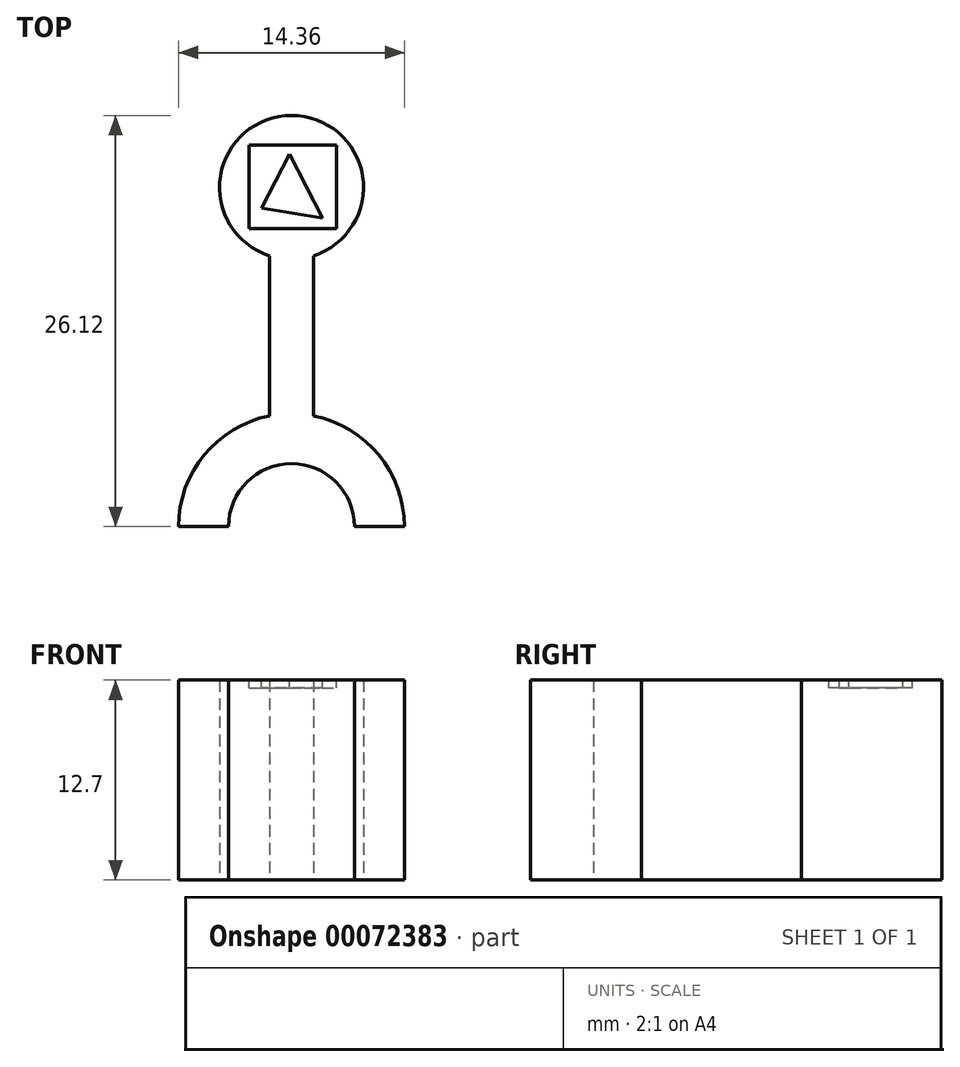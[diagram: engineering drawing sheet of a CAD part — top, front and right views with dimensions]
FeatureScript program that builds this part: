
annotation { "Feature Type Name" : "Feature", "Feature Type Description" : "" }
export const myFeature = defineFeature(function(context is Context, id is Id, definition is map)
    precondition{}
    {
        {
            var Q0;
            Q0=qCreatedBy(makeId("Top.planeOp"),FACE);
            var sketch = newSketch(context, id + "F0", { "sketchPlane" : qUnion([Q0])});
            skArc(sketch, "E0", {"start": v(4, 0) * mm, "mid": v(0, 4) * mm, "end": v(-4, 0) * mm});
            skArc(sketch, "E1", {"start": v(7.18, 0) * mm, "mid": v(0, 7.18) * mm, "end": v(-7.18, 0) * mm});
            skLineSegment(sketch, "E2", {"start": v(-7.18, 0) * mm, "end": v(-4, 0) * mm});
            skLineSegment(sketch, "E3", {"start": v(4, 0) * mm, "end": v(7.18, 0) * mm});
            skCircle(sketch, "E4", {"center": v(0, 21.55) * mm, "radius": 4.57 * mm});
            skLineSegment(sketch, "E5.rect.bottom", {"start": v(1.4, 7.04) * mm, "end": v(-1.4, 7.04) * mm, "construction": true});
            skLineSegment(sketch, "E5.rect.top", {"start": v(1.4, 17.2) * mm, "end": v(-1.4, 17.2) * mm, "construction": true});
            skLineSegment(sketch, "E5.rect.left", {"start": v(1.4, 7.04) * mm, "end": v(1.4, 17.2) * mm});
            skLineSegment(sketch, "E5.rect.right", {"start": v(-1.4, 7.04) * mm, "end": v(-1.4, 17.2) * mm});
            skPoint(sketch, "E5.rect.middle", {"position": v(0, 12.12) * mm});
            skSolve(sketch);
        }
        {
            var Q0;
            Q0=qSketchRegion(id+"F0",true);
            extrude(context, id + "F1", {"entities" : qUnion([Q0]), "depth" : 12.7 * mm});
        }
        {
            var Q0;
            Q0=qCreatedBy(makeId("Top.planeOp"),FACE);
            var Q1;
            Q1=makeQuery(id+"F1.opExtrude","CAP_FACE",FACE,{"disambiguationData":[OSD([sQuery(id+"F0.wireOp",EDGE,"E0"),sQuery(id+"F0.wireOp",EDGE,"E1"),sQuery(id+"F0.wireOp",EDGE,"E2"),sQuery(id+"F0.wireOp",EDGE,"E3"),sQuery(id+"F0.wireOp",EDGE,"E4"),sQuery(id+"F0.wireOp",EDGE,"E5.rect.left"),sQuery(id+"F0.wireOp",EDGE,"E5.rect.right")])],"isStart":false});
            cPlane(context, id + "F2", {"entities" : qUnion([Q0, Q1]), "cplaneType" : CPlaneType.MID_PLANE, "offset" : 152.4 * mm, "width" : 152.4 * mm, "height" : 152.4 * mm});
        }
        {
            var Q0;
            Q0=qCreatedBy(id+"F2.planeOp",FACE);
            cPlane(context, id + "F3", {"entities" : qUnion([Q0]), "cplaneType" : CPlaneType.OFFSET, "offset" : 6.35 * mm, "width" : 152.4 * mm, "height" : 152.4 * mm});
        }
        {
            var Q0;
            Q0=qCreatedBy(id+"F2.planeOp",FACE);
            cPlane(context, id + "F4", {"entities" : qUnion([Q0]), "cplaneType" : CPlaneType.OFFSET, "offset" : 6.35 * mm, "oppositeDirection" : true, "width" : 152.4 * mm, "height" : 152.4 * mm});
        }
        {
            var Q0;
            Q0=makeQuery(id+"F1.opExtrude","CAP_FACE",FACE,{"disambiguationData":[OSD([sQuery(id+"F0.wireOp",EDGE,"E0"),sQuery(id+"F0.wireOp",EDGE,"E1"),sQuery(id+"F0.wireOp",EDGE,"E2"),sQuery(id+"F0.wireOp",EDGE,"E3"),sQuery(id+"F0.wireOp",EDGE,"E4"),sQuery(id+"F0.wireOp",EDGE,"E5.rect.left"),sQuery(id+"F0.wireOp",EDGE,"E5.rect.right")])],"isStart":false});
            var sketch = newSketch(context, id + "F5", { "sketchPlane" : qUnion([Q0])});
            skLineSegment(sketch, "E6", {"start": v(-1.9, 20.24) * mm, "end": v(-0.12, 23.65) * mm});
            skLineSegment(sketch, "E7", {"start": v(-0.12, 23.65) * mm, "end": v(1.97, 19.62) * mm});
            skLineSegment(sketch, "E8", {"start": v(1.97, 19.62) * mm, "end": v(-1.9, 20.24) * mm});
            skLineSegment(sketch, "E9.bottom", {"start": v(-2.69, 24.25) * mm, "end": v(2.85, 24.25) * mm});
            skLineSegment(sketch, "E9.top", {"start": v(-2.69, 18.94) * mm, "end": v(2.85, 18.94) * mm});
            skLineSegment(sketch, "E9.left", {"start": v(-2.69, 24.25) * mm, "end": v(-2.69, 18.94) * mm});
            skLineSegment(sketch, "E9.right", {"start": v(2.85, 24.25) * mm, "end": v(2.85, 18.94) * mm});
            skSolve(sketch);
        }
        {
            var Q0;
            Q0=makeQuery(id+"F5.imprint","IMPRINT",FACE,{"disambiguationData":[TD([[makeQuery(id+"F5.imprint","IMPRINT",EDGE,{"derivedFrom":sQuery(id+"F5.wireOp",EDGE,"E6")}),1.0]])]});
            extrude(context, id + "F6", {"entities" : qUnion([Q0]), "operationType" : NewBodyOperationType.REMOVE, "oppositeDirection" : true, "depth" : 0.5 * mm});
        }
    });
